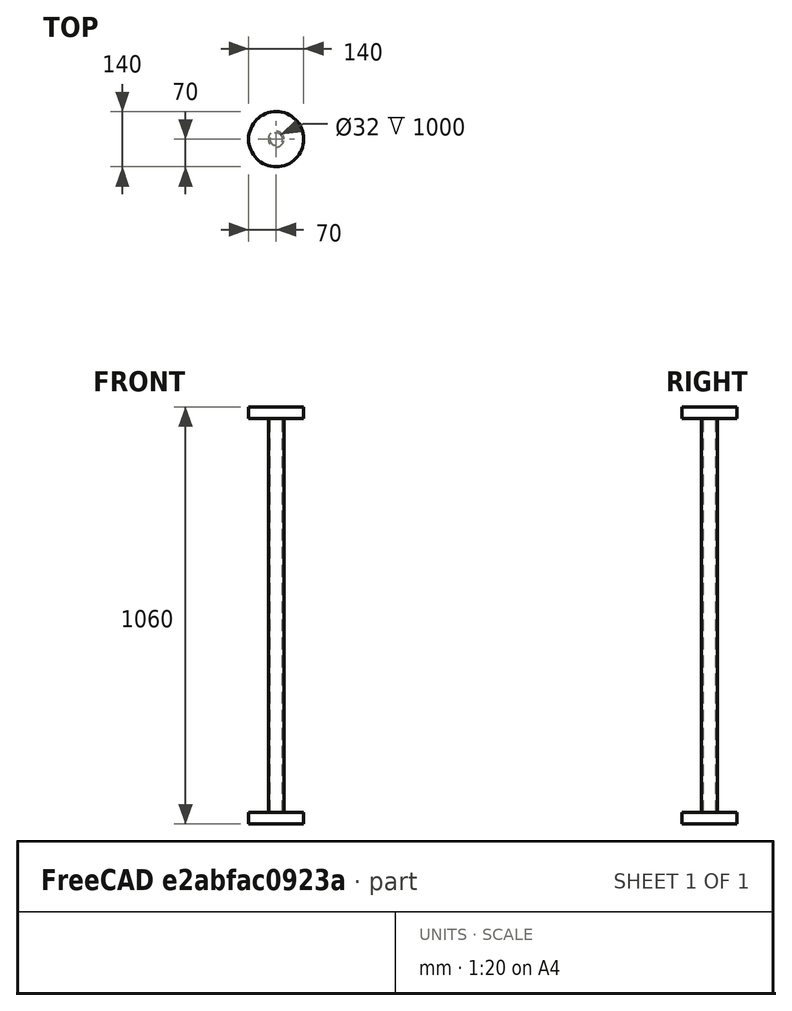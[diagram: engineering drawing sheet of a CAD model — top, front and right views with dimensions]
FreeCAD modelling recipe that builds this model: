
FCSTD DOCUMENT  (FreeCAD 0.19R)
Label: model
License: All rights reserved
LicenseURL: http://en.wikipedia.org/wiki/All_rights_reserved
objects: Mesh::Feature×3, Part::Cylinder×2, Part::FeaturePython×1
note: 3 computed .brp shape members not serialized (recipe doc carries the construction recipe); baked Part::Feature solids carry a one-line shape summary decoded from their .brp

FEATURE [Part::FeaturePython] Tube  # WARN: FeaturePython — macro-defined, semantics opaque (R4)
  AttacherType = Attacher::AttachEngine3D
  Height = 1000
  InnerRadius = 16
  OuterRadius = 20
FEATURE [Part::Cylinder] Cylinder001
  Angle = 360
  AttacherType = Attacher::AttachEngine3D
  Height = 30
  Placement = pos=(0,0,-30) rot=(0,0,1;0rad)
  Radius = 70
FEATURE [Part::Cylinder] Cylinder003
  Angle = 360
  AttacherType = Attacher::AttachEngine3D
  Height = 30
  Placement = pos=(0,0,1000) rot=(0,0,1;0rad)
  Radius = 70
FEATURE [Mesh::Feature] Mesh001  label="Cylinder001 (Meshed)"
FEATURE [Mesh::Feature] Mesh002  label="Cylinder003 (Meshed)"
FEATURE [Mesh::Feature] Mesh  label="Tube (Meshed)"
